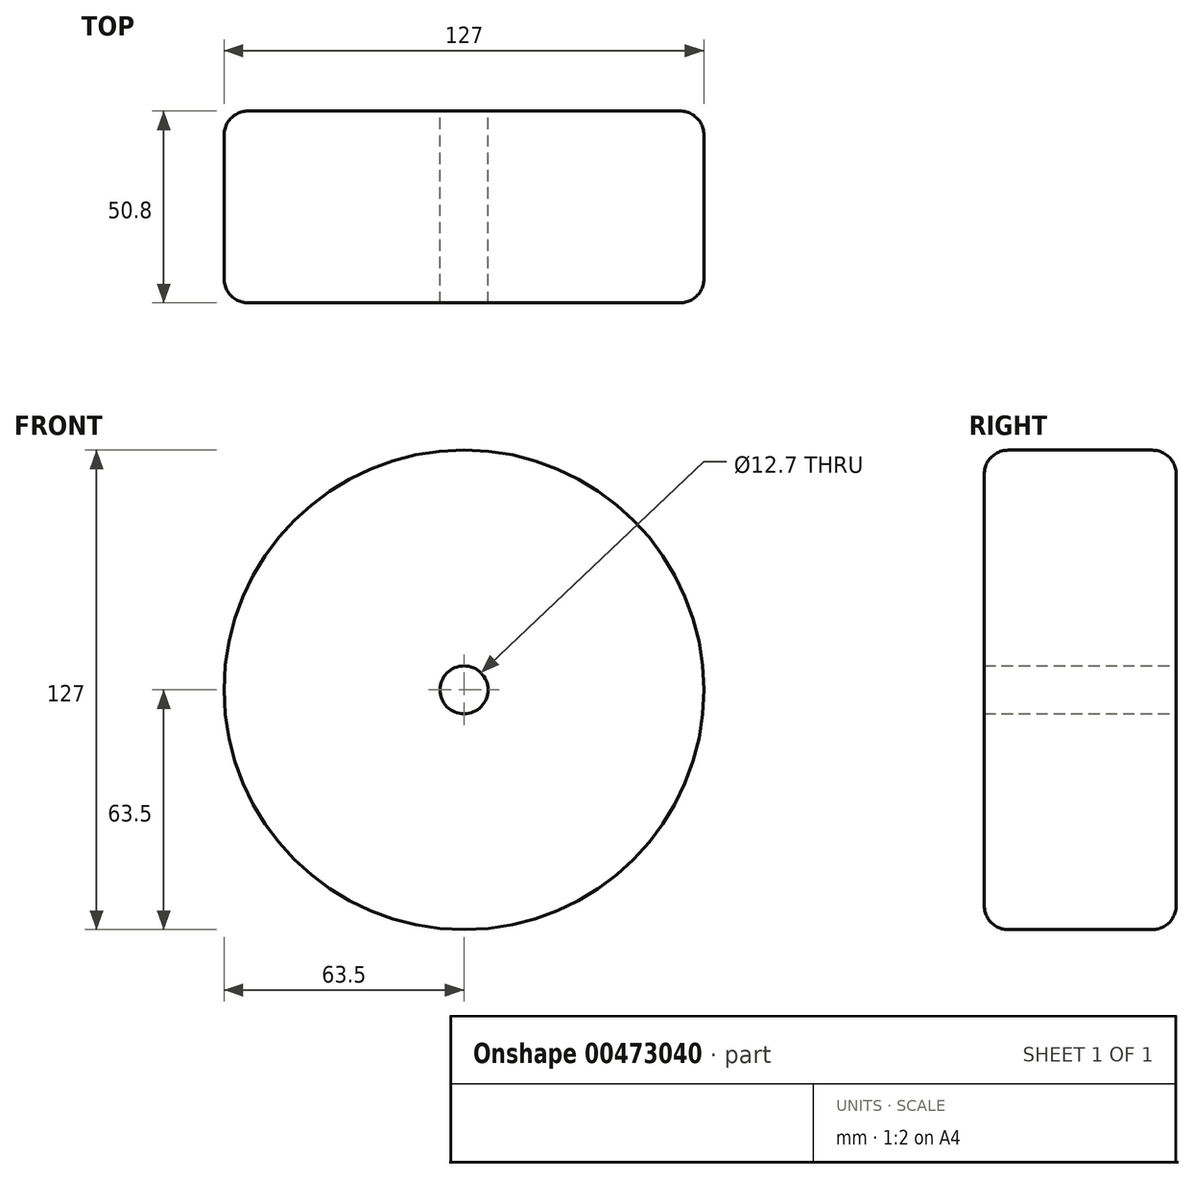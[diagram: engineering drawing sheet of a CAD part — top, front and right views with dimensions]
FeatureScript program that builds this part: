
annotation { "Feature Type Name" : "Feature", "Feature Type Description" : "" }
export const myFeature = defineFeature(function(context is Context, id is Id, definition is map)
    precondition{}
    {
        {
            var Q0;
            Q0=qCreatedBy(makeId("Front.planeOp"),FACE);
            var sketch = newSketch(context, id + "F0", { "sketchPlane" : qUnion([Q0])});
            skCircle(sketch, "E0", {"center": v(0, 0) * mm, "radius": 6.35 * mm});
            skCircle(sketch, "E1", {"center": v(0, 0) * mm, "radius": 63.5 * mm});
            skSolve(sketch);
        }
        {
            var Q0;
            Q0 = qSketchRegion(id + "F0", true);
            var Q1;
            Q1=makeQuery(id+"F0.imprint","IMPRINT",FACE,{"disambiguationData":[TD([[makeQuery(id+"F0.imprint","IMPRINT",EDGE,{"derivedFrom":sQuery(id+"F0.wireOp",EDGE,"E0")}),-1.0]])]});
            extrude(context, id + "F1", {"entities" : qUnion([Q0, Q1]), "depth" : 50.8 * mm});
        }
        {
            var Q0;
            Q0=makeQuery(id+"F1.opExtrude","CAP_EDGE",EDGE,{"disambiguationData":[OSD([sQuery(id+"F0.wireOp",EDGE,"E1")])],"isStart":false});
            var Q1;
            Q1=makeQuery(id+"F1.opExtrude","CAP_EDGE",EDGE,{"disambiguationData":[OSD([sQuery(id+"F0.wireOp",EDGE,"E1")])],"isStart":true});
            fillet(context, id + "F2", {"entities" : qUnion([Q0, Q1]), "radius" : 6.35 * mm, "tangentPropagation" : true, "allowEdgeOverflow" : false});
        }
    });
